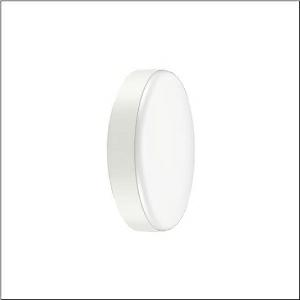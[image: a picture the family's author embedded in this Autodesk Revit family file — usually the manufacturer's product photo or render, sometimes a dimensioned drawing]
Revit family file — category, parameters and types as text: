
# Revit family: round_31_51wc10mb44a
name_source: partatom
category: Lighting Fixtures
units: mm (PartAtom-declared; Revit-internal decimal feet)

## family parameters
Cut with Voids When Loaded = No
Host = Face
Light Source = No
Part Type = Normal
Room Calculation Point = No
Round Connector Dimension = Use Diameter
Shared = No

## types (1)
- --- (1 x LED, 4400 lm, 34 W, 4000K)
    Apparent Load = 34 VA
    CIE Flux Codes = 44 75 94 94 100
    Color Rendering = 80
    Color Temperature = 4000K
    Default Elevation = 1800 mm
    Description = Round 31, wall and ceiling luminaire, primary optical cover: cover, of PC, opal, light emission: direct distribution, primary light characteristic: symmetric, installation type: surface-mounted, LED, rated luminous flux: 4.400lm, luminous efficacy: 129lm/W, light colour: 840, colour temperature: 4000K, control gear: ON/OFF Multilumen, with terminal, 3-pole, max. 2.5mm², mains connection: 220..240V, AC, 50/60Hz, rated input power: 34W, luminaire housing, of PC, traffic white (RAL 9016), diameter: 480mm, protection rating (complete): IP65, insulation class (complete): insulation class II (safety insulation), certification: CE, impact resistance: IK10, permissible operating ambient temperature: -20..+40°C, permissible storage temperature: -20..+60°C, packaging unit: 1 piece
    Height = 97 mm
    Lamp = 1 x LED
    Lamp Light Flux = 4400 lm
    Lamp Power = 34 W
    Lamp count = 1
    Length = 480 mm
    Luminous efficacy = 129 lm/W
    Manufacturer = Siteco
    ModVariant = No
    Model = 51WC10MB44A
    Mounting Place = Wall
    Mounting Type = Surface mounted
    Number of Poles = 1
    OnlyDefault = Yes
    Power Factor = 1
    Product Name = Round 31
    Product group = wall and ceiling luminaire | wall mounted
    ProductGroupID = 2001
    Protection Class = Protection class II
    Protection Degree = IP 65
    RLX_Detail_Level = 1
    RLX_Emergency_Light_Flux = 0 lm
    RLX_Emergency_Type = 0
    RLX_Emergency_Type_DB = No
    RlxData = <blob elided: 56433 chars, md5=2c78988b>
    Socket = socket
    Standby Power = 0 W
    System Light Flux = 4400 lm
    System Power = 34 W
    Type Comments = factory setting: luminous flux: 100 % | (ON | ON)
    Type Image = l_1007188.jpg
    URL = http://relux.com
    VarID = @adj_150301
    Voltage = 0 V
    Weight = 0.00 kg
    Width = 0 mm  [stored 0 ft]

note: [stored X ft] marks values corroborated as IEEE doubles in the binary element streams (Revit-internal decimal feet)

## geometry (parser evidence)
native form markers: Blend x4, Sweep x12
no freeform markers — native parametric forms only
